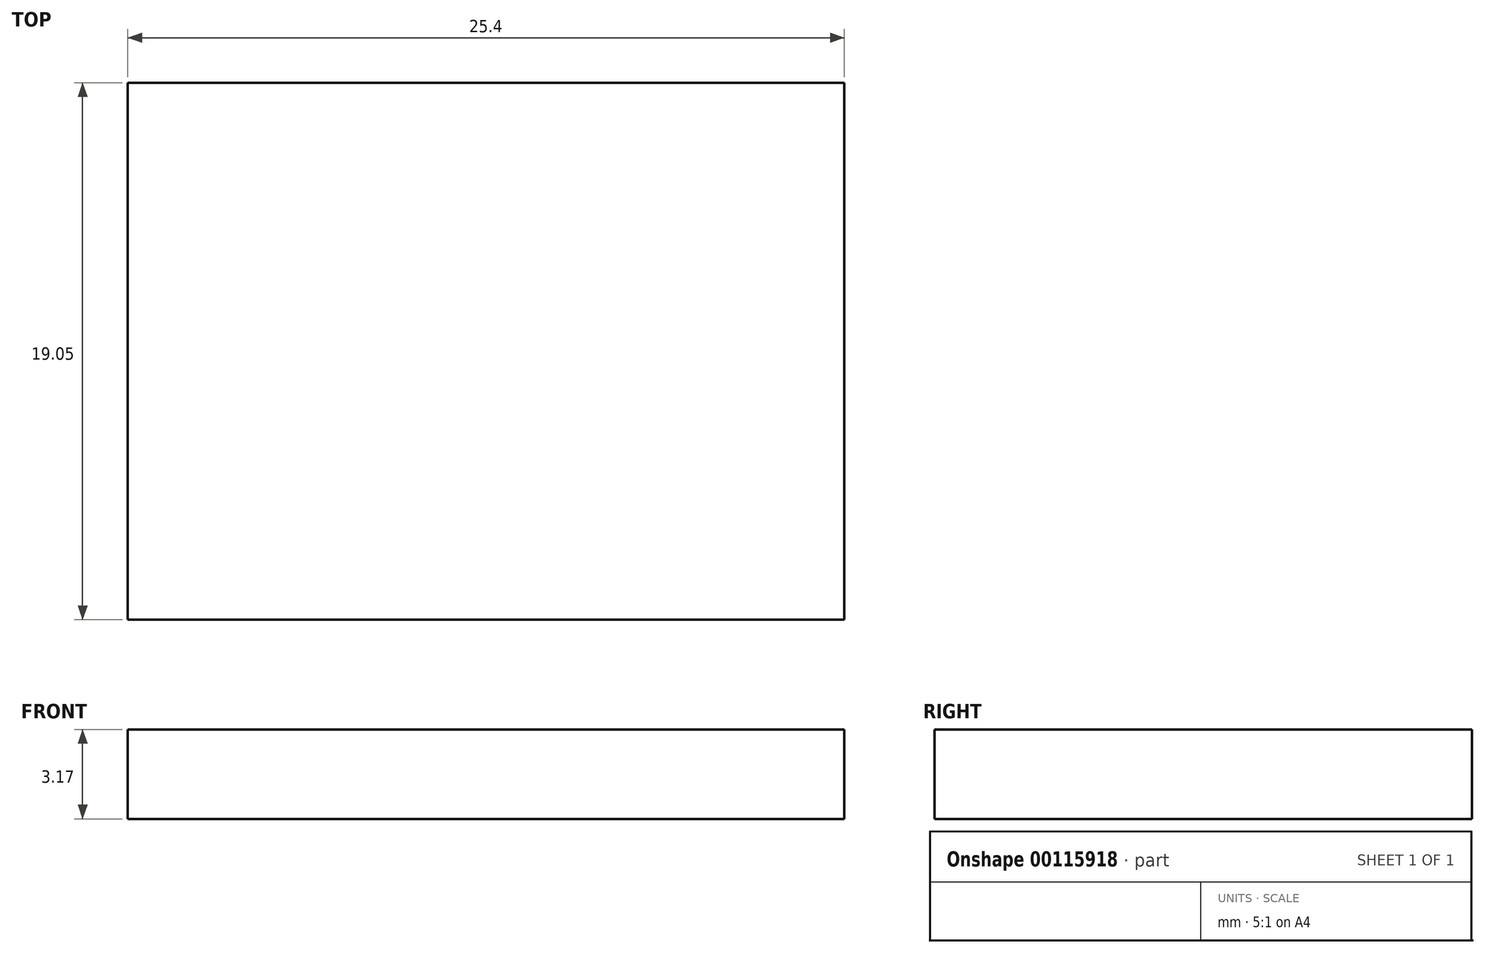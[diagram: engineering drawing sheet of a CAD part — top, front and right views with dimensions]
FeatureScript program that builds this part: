
annotation { "Feature Type Name" : "Feature", "Feature Type Description" : "" }
export const myFeature = defineFeature(function(context is Context, id is Id, definition is map)
    precondition{}
    {
        {
            var Q0;
            Q0=qCreatedBy(makeId("Top.planeOp"),FACE);
            var sketch = newSketch(context, id + "F0", { "sketchPlane" : qUnion([Q0])});
            skLineSegment(sketch, "E0.bottom", {"start": v(-19.7, 17.3) * mm, "end": v(5.7, 17.3) * mm});
            skLineSegment(sketch, "E0.top", {"start": v(-19.7, -1.75) * mm, "end": v(5.7, -1.75) * mm});
            skLineSegment(sketch, "E0.left", {"start": v(-19.7, 17.3) * mm, "end": v(-19.7, -1.75) * mm});
            skLineSegment(sketch, "E0.right", {"start": v(5.7, 17.3) * mm, "end": v(5.7, -1.75) * mm});
            skSolve(sketch);
        }
        {
            var Q0;
            Q0=makeQuery(id+"F0.imprint","IMPRINT",FACE,{"disambiguationData":[TD([[makeQuery(id+"F0.imprint","IMPRINT",EDGE,{"derivedFrom":sQuery(id+"F0.wireOp",EDGE,"E0.bottom")}),-1.0]])]});
            extrude(context, id + "F1", {"entities" : qUnion([Q0]), "depth" : 3.17 * mm});
        }
    });
